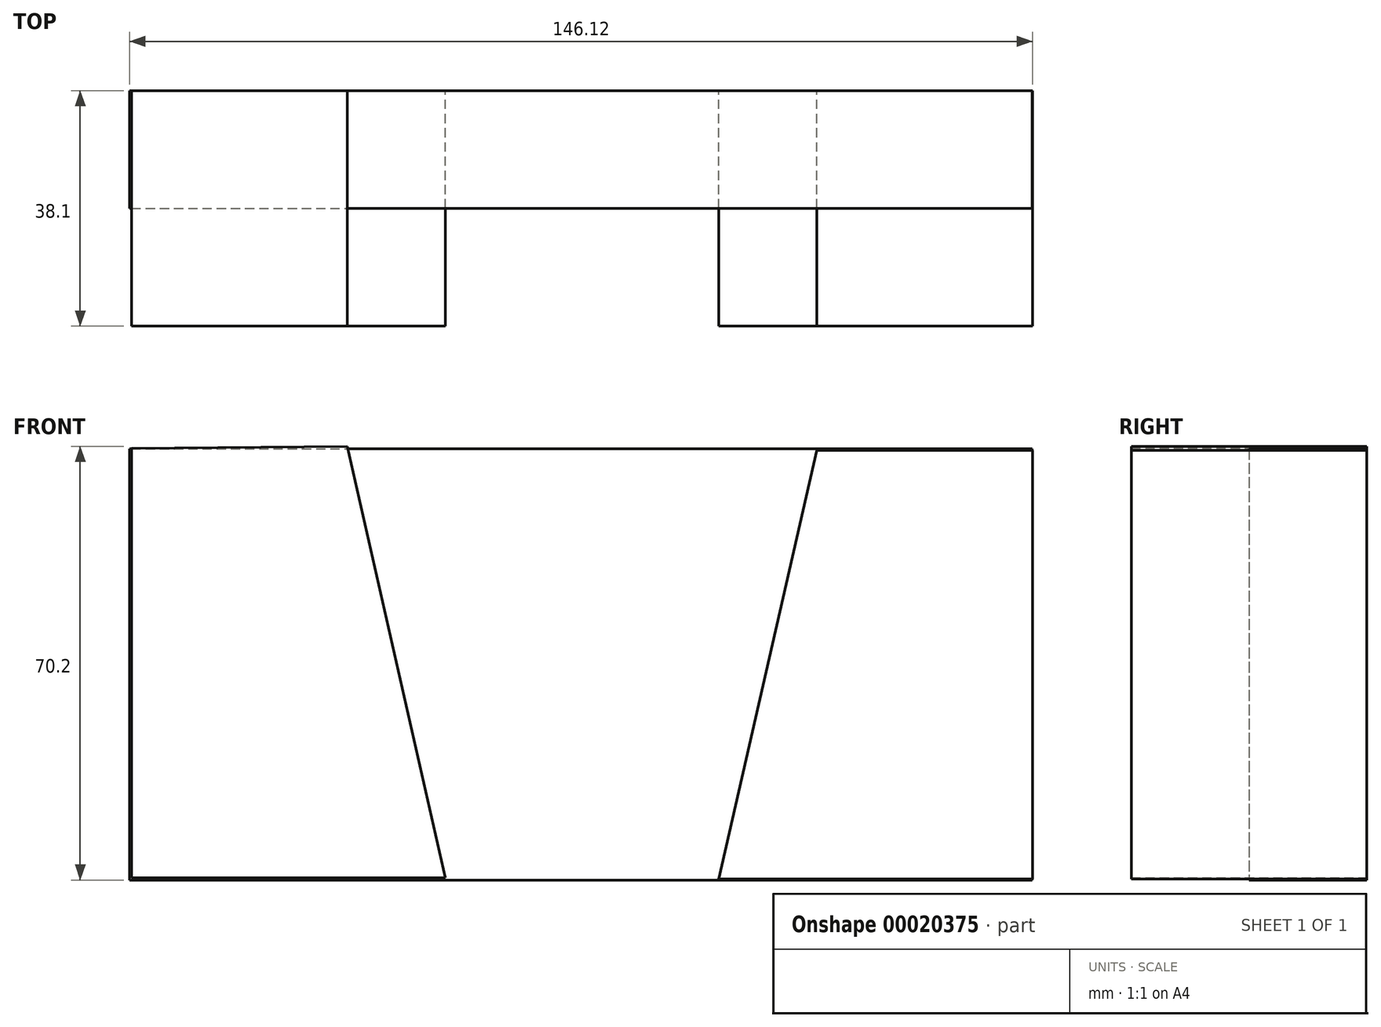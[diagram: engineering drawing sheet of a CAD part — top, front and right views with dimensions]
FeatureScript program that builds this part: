
annotation { "Feature Type Name" : "Feature", "Feature Type Description" : "" }
export const myFeature = defineFeature(function(context is Context, id is Id, definition is map)
    precondition{}
    {
        {
            var Q0;
            Q0=qCreatedBy(makeId("Front.planeOp"),FACE);
            var sketch = newSketch(context, id + "F0", { "sketchPlane" : qUnion([Q0])});
            skLineSegment(sketch, "E0.bottom", {"start": v(-70.77, 31.19) * mm, "end": v(75.28, 31.19) * mm});
            skLineSegment(sketch, "E0.top", {"start": v(-70.77, -38.66) * mm, "end": v(75.28, -38.66) * mm});
            skLineSegment(sketch, "E0.left", {"start": v(-70.77, 31.19) * mm, "end": v(-70.77, -38.66) * mm});
            skLineSegment(sketch, "E0.right", {"start": v(75.28, 31.19) * mm, "end": v(75.28, -38.66) * mm});
            skSolve(sketch);
        }
        {
            var Q0;
            Q0=qCreatedBy(makeId("Front.planeOp"),FACE);
            var sketch = newSketch(context, id + "F1", { "sketchPlane" : qUnion([Q0])});
            skLineSegment(sketch, "E1", {"start": v(-70.5, 31.26) * mm, "end": v(-70.5, -38.31) * mm});
            skLineSegment(sketch, "E2", {"start": v(-70.5, -38.31) * mm, "end": v(-35.58, -38.31) * mm});
            skLineSegment(sketch, "E3", {"start": v(-70.5, 31.26) * mm, "end": v(-35.58, 31.54) * mm});
            skLineSegment(sketch, "E4", {"start": v(-35.58, -38.31) * mm, "end": v(-53.04, -38.31) * mm});
            skLineSegment(sketch, "E5", {"start": v(-35.58, -38.31) * mm, "end": v(-19.7, -38.31) * mm});
            skLineSegment(sketch, "E6", {"start": v(-19.7, -38.31) * mm, "end": v(-35.58, 31.54) * mm});
            skLineSegment(sketch, "E7.bottom", {"start": v(40.43, 30.9) * mm, "end": v(75.35, 30.9) * mm});
            skLineSegment(sketch, "E7.top", {"start": v(40.43, -38.52) * mm, "end": v(75.35, -38.52) * mm});
            skLineSegment(sketch, "E7.right", {"start": v(75.35, 30.9) * mm, "end": v(75.35, -38.52) * mm});
            skLineSegment(sketch, "E8", {"start": v(40.43, -38.52) * mm, "end": v(24.55, -38.52) * mm});
            skLineSegment(sketch, "E9", {"start": v(24.55, -38.52) * mm, "end": v(40.43, 30.9) * mm});
            skSolve(sketch);
        }
        {
            var Q0;
            Q0=makeQuery(id+"F1.imprint","IMPRINT",FACE,{"disambiguationData":[TD([[makeQuery(id+"F1.imprint","IMPRINT",EDGE,{"derivedFrom":sQuery(id+"F1.wireOp",EDGE,"E1")}),1.0]])]});
            var Q1;
            Q1=makeQuery(id+"F1.imprint","IMPRINT",FACE,{"disambiguationData":[TD([[makeQuery(id+"F1.imprint","IMPRINT",EDGE,{"derivedFrom":sQuery(id+"F1.wireOp",EDGE,"E7.bottom")}),-1.0]])]});
            extrude(context, id + "F2", {"entities" : qUnion([Q0, Q1]), "depth" : 38.1 * mm});
        }
        {
            var Q0;
            Q0=makeQuery(id+"F0.imprint","IMPRINT",FACE,{"disambiguationData":[TD([[makeQuery(id+"F0.imprint","IMPRINT",EDGE,{"derivedFrom":sQuery(id+"F0.wireOp",EDGE,"E0.bottom")}),-1.0]])]});
            extrude(context, id + "F3", {"entities" : qUnion([Q0]), "depth" : 19.05 * mm});
        }
    });
